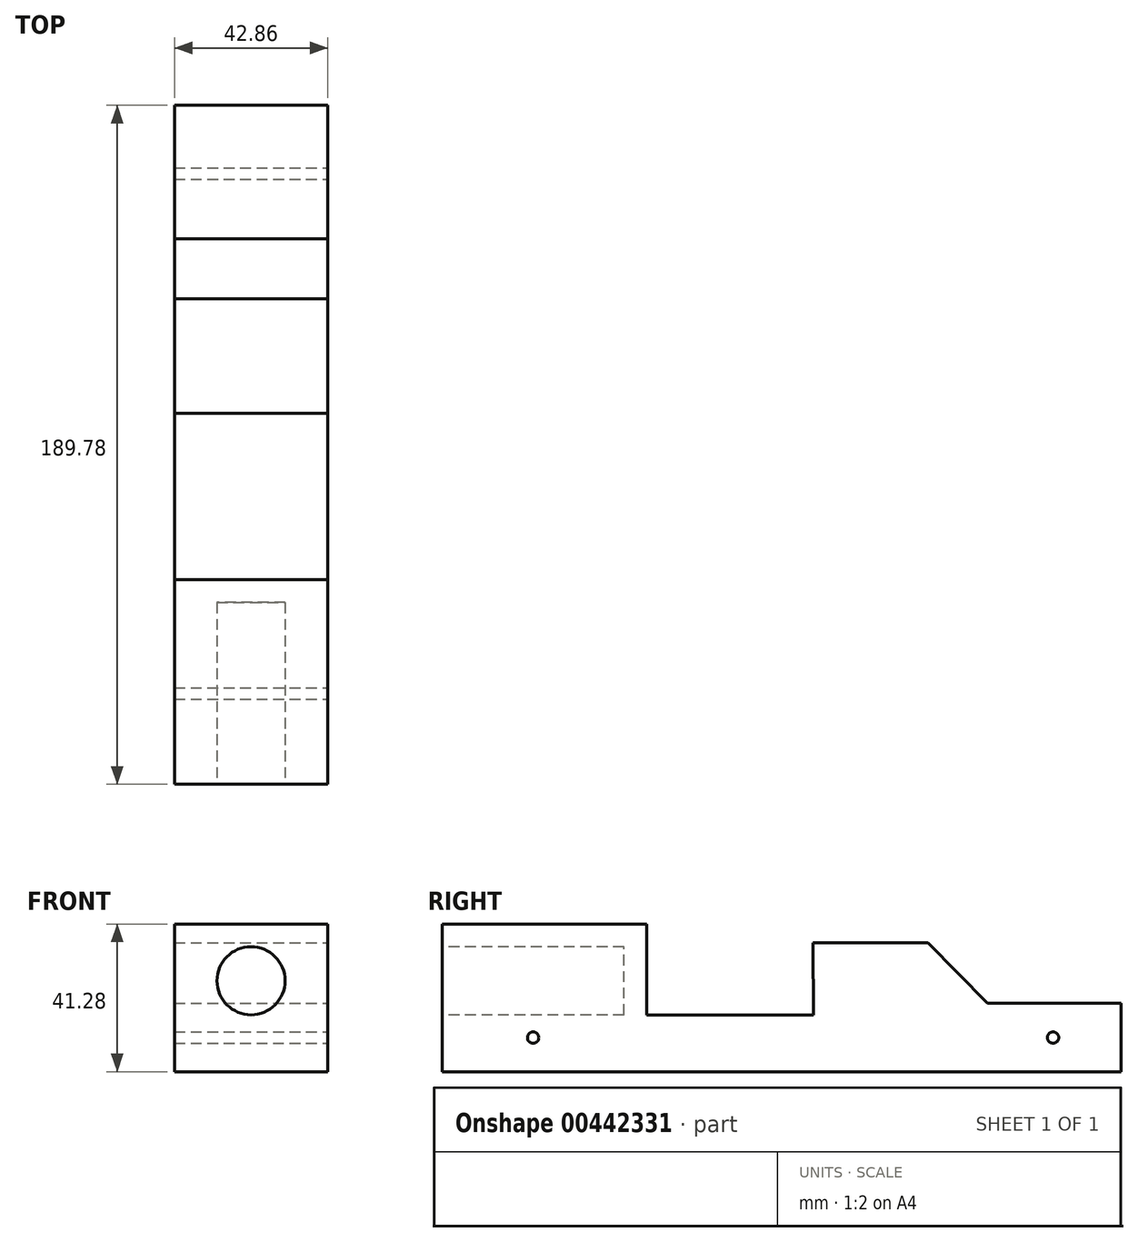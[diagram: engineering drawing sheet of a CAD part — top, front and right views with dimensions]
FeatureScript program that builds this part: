
annotation { "Feature Type Name" : "Feature", "Feature Type Description" : "" }
export const myFeature = defineFeature(function(context is Context, id is Id, definition is map)
    precondition{}
    {
        {
            var Q0;
            Q0=qCreatedBy(makeId("Right.planeOp"),FACE);
            var sketch = newSketch(context, id + "F0", { "sketchPlane" : qUnion([Q0])});
            skLineSegment(sketch, "E0", {"start": v(-152.4, 0) * mm, "end": v(152.4, 0) * mm});
            skLineSegment(sketch, "E1", {"start": v(-152.4, 0) * mm, "end": v(-152.4, 69.85) * mm});
            skLineSegment(sketch, "E2", {"start": v(152.4, 0) * mm, "end": v(152.4, 19.05) * mm});
            skLineSegment(sketch, "E3", {"start": v(152.4, 19.05) * mm, "end": v(-152.4, 69.85) * mm});
            skPoint(sketch, "E4.endSnap0", {"position": v(-152.4, 34.93) * mm});
            skLineSegment(sketch, "E5.0", {"start": v(-95.25, 50.8) * mm, "end": v(-152.4, 50.8) * mm, "construction": true});
            skLineSegment(sketch, "E5.1", {"start": v(-95.25, 50.8) * mm, "end": v(-95.25, 19.05) * mm, "construction": true});
            skLineSegment(sketch, "E5.2", {"start": v(-95.25, 19.05) * mm, "end": v(-152.4, 19.05) * mm, "construction": true});
            skSolve(sketch);
        }
        {
            var Q0;
            Q0=makeQuery(id+"F0.imprint","IMPRINT",FACE,{"disambiguationData":[TD([[makeQuery(id+"F0.imprint","IMPRINT",EDGE,{"derivedFrom":sQuery(id+"F0.wireOp",EDGE,"E0")}),1.0]])]});
            extrude(context, id + "F1", {"entities" : qUnion([Q0]), "depth" : 42.86 * mm, "symmetric" : true});
        }
        {
            var Q0;
            Q0=makeQuery(id+"F1.opExtrude","SWEPT_FACE",FACE,{"disambiguationData":[OSD([sQuery(id+"F0.wireOp",EDGE,"E1")])]});
            var sketch = newSketch(context, id + "F2", { "sketchPlane" : qUnion([Q0])});
            skLineSegment(sketch, "E6", {"start": v(21.43, 34.93) * mm, "end": v(0, 34.93) * mm, "construction": true});
            skCircle(sketch, "E7", {"center": v(0, 34.93) * mm, "radius": 9.53 * mm});
            skSolve(sketch);
        }
        {
            var Q0;
            Q0=makeQuery(id+"F2.imprint","IMPRINT",FACE,{"disambiguationData":[TD([[makeQuery(id+"F2.imprint","IMPRINT",EDGE,{"derivedFrom":sQuery(id+"F2.wireOp",EDGE,"E7")}),1.0]])]});
            var Q1;
            Q1=sQuery(id+"F2.wireOp",EDGE,"E7");
            extrude(context, id + "F3", {"entities" : qUnion([Q0]), "operationType" : NewBodyOperationType.REMOVE, "surfaceEntities" : qUnion([Q1]), "oppositeDirection" : true, "depth" : 50.8 * mm});
        }
        {
            var Q0;
            Q0=makeQuery(id+"F1.opExtrude","CAP_FACE",FACE,{"disambiguationData":[OSD([sQuery(id+"F0.wireOp",EDGE,"E0"),sQuery(id+"F0.wireOp",EDGE,"E1"),sQuery(id+"F0.wireOp",EDGE,"E2"),sQuery(id+"F0.wireOp",EDGE,"E3")])],"isStart":false});
            var sketch = newSketch(context, id + "F4", { "sketchPlane" : qUnion([Q0])});
            skLineSegment(sketch, "E8", {"start": v(-152.4, 34.93) * mm, "end": v(-152.4, 44.45) * mm, "construction": true});
            skLineSegment(sketch, "E9.0", {"start": v(-95.25, 19.05) * mm, "end": v(-152.4, 19.05) * mm, "construction": true});
            skLineSegment(sketch, "E9.1", {"start": v(-95.25, 50.8) * mm, "end": v(-95.25, 19.05) * mm, "construction": true});
            skLineSegment(sketch, "E9.2", {"start": v(-152.4, 50.8) * mm, "end": v(-95.25, 50.8) * mm, "construction": true});
            skLineSegment(sketch, "E10", {"start": v(37.38, 0) * mm, "end": v(37.38, 9.53) * mm, "construction": true});
            skLineSegment(sketch, "E11", {"start": v(-152.4, 44.45) * mm, "end": v(-101.6, 44.45) * mm, "construction": true});
            skLineSegment(sketch, "E12", {"start": v(-101.6, 44.45) * mm, "end": v(-101.6, 25.4) * mm, "construction": true});
            skLineSegment(sketch, "E13", {"start": v(-101.6, 25.4) * mm, "end": v(-152.4, 25.4) * mm, "construction": true});
            skLineSegment(sketch, "E14", {"start": v(-48.73, 45.53) * mm, "end": v(-48.73, 25.4) * mm});
            skLineSegment(sketch, "E15", {"start": v(-95.25, 25.4) * mm, "end": v(-48.59, 25.4) * mm});
            skLineSegment(sketch, "E16", {"start": v(-48.73, 45.53) * mm, "end": v(-16.65, 45.53) * mm});
            skLineSegment(sketch, "E17", {"start": v(-152.4, 50.8) * mm, "end": v(-95.25, 50.8) * mm});
            skLineSegment(sketch, "E18", {"start": v(-95.25, 50.8) * mm, "end": v(-95.25, 25.4) * mm});
            skLineSegment(sketch, "E19", {"start": v(-48.59, 25.4) * mm, "end": v(-48.73, 45.53) * mm});
            skLineSegment(sketch, "E20", {"start": v(-16.65, 45.53) * mm, "end": v(-48.73, 45.53) * mm});
            skLineSegment(sketch, "E21", {"start": v(37.38, 28.62) * mm, "end": v(37.38, 0) * mm});
            skLineSegment(sketch, "E22", {"start": v(37.38, 0) * mm, "end": v(-152.4, 0) * mm});
            skLineSegment(sketch, "E23", {"start": v(-152.4, 50.8) * mm, "end": v(-152.4, 0) * mm});
            skLineSegment(sketch, "E24", {"start": v(-152.4, 0) * mm, "end": v(37.38, 0) * mm});
            skPoint(sketch, "E25.endSnap0", {"position": v(-127, 25.4) * mm});
            skLineSegment(sketch, "E26", {"start": v(-152.4, 9.52) * mm, "end": v(37.38, 9.53) * mm});
            skLineSegment(sketch, "E27", {"start": v(-152.4, 9.52) * mm, "end": v(-127, 9.52) * mm});
            skLineSegment(sketch, "E28", {"start": v(-127, 9.52) * mm, "end": v(-127, 19.05) * mm});
            skLineSegment(sketch, "E29", {"start": v(37.38, 9.53) * mm, "end": v(18.33, 9.53) * mm});
            skLineSegment(sketch, "E30", {"start": v(18.33, 9.53) * mm, "end": v(18.33, 19.05) * mm});
            skCircle(sketch, "E31", {"center": v(18.33, 19.05) * mm, "radius": 1.59 * mm});
            skCircle(sketch, "E32", {"center": v(-127, 19.05) * mm, "radius": 1.59 * mm});
            skLineSegment(sketch, "E33", {"start": v(-48.73, 28.63) * mm, "end": v(-48.61, 28.63) * mm});
            skPoint(sketch, "E34.orphan", {"position": v(0, 28.62) * mm});
            skLineSegment(sketch, "E35", {"start": v(0, 28.62) * mm, "end": v(37.38, 28.62) * mm});
            skLineSegment(sketch, "E36", {"start": v(-16.65, 45.53) * mm, "end": v(0, 28.62) * mm});
            skSolve(sketch);
        }
        {
            var Q0;
            Q0=makeQuery(id+"F4.imprint","IMPRINT",FACE,{"disambiguationData":[TD([[makeQuery(id+"F4.imprint","IMPRINT",EDGE,{"derivedFrom":sQuery(id+"F4.wireOp",EDGE,"E17")}),-1.0]])]});
            extrude(context, id + "F5", {"entities" : qUnion([Q0]), "operationType" : NewBodyOperationType.INTERSECT, "endBound" : BoundingType.THROUGH_ALL, "oppositeDirection" : true, "depth" : 25.4 * mm});
        }
    });
